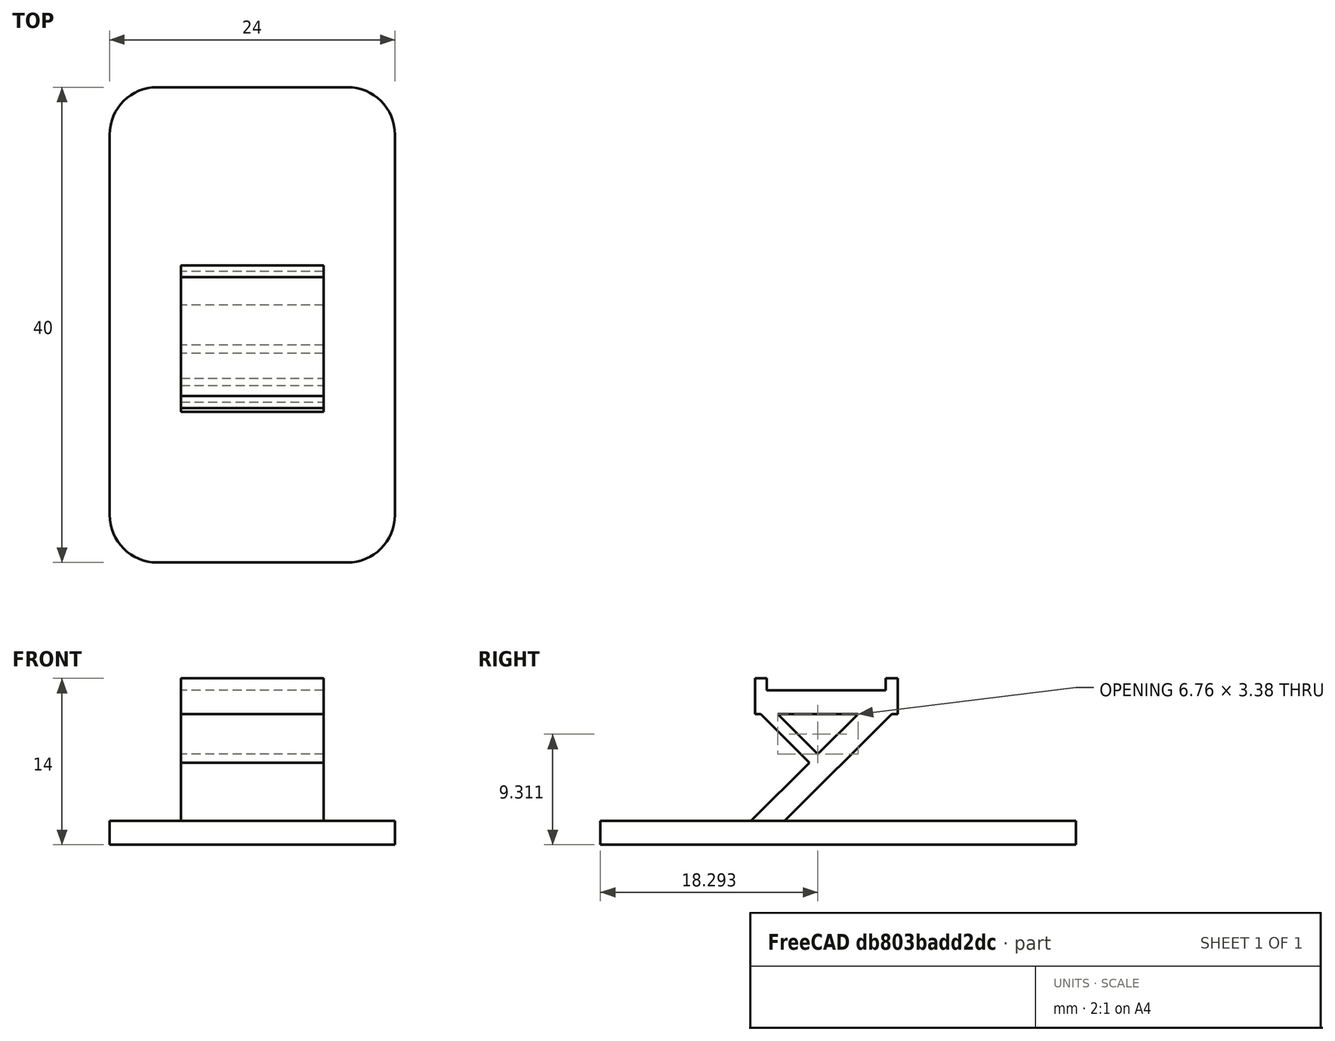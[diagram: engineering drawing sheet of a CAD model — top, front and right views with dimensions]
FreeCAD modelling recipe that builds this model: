
FCSTD DOCUMENT  (FreeCAD 0.17R13528 (Git))
Label: soporte
License: All rights reserved
LicenseURL: http://en.wikipedia.org/wiki/All_rights_reserved
objects: Part::Box×6, Mesh::Feature×1, Part::MultiFuse×1, Part::Fillet×1
note: 8 computed .brp shape members not serialized (recipe doc carries the construction recipe); baked Part::Feature solids carry a one-line shape summary decoded from their .brp

FEATURE [Part::Box] Box  label="Cubo"
  AttacherType = Attacher::AttachEngine3D
  Height = 2
  Length = 12
  Placement = pos=(-6,30.3,3.5) rot=(1,0,0;0.785398rad)
  Width = 15
FEATURE [Mesh::Feature] nave_simple
  Placement = pos=(0,0,26) rot=(1,0,0;-1.5708rad)
FEATURE [Part::Box] Box001  label="Cubo001"
  AttacherType = Attacher::AttachEngine3D
  Height = 2
  Length = 12
  Placement = pos=(-6,29.3,15) rot=(0,0,1;0rad)
  Width = 1
FEATURE [Part::Box] Box002  label="Cubo002"
  AttacherType = Attacher::AttachEngine3D
  Height = 2
  Length = 12
  Placement = pos=(-6,40.3,15) rot=(0,0,1;0rad)
  Width = 1
FEATURE [Part::Box] Box003  label="Cubo003"
  AttacherType = Attacher::AttachEngine3D
  Height = 2
  Length = 12
  Placement = pos=(-6,29.3,14) rot=(0,0,1;0rad)
  Width = 12
FEATURE [Part::Box] Box004  label="Cubo004"
  AttacherType = Attacher::AttachEngine3D
  Height = 2
  Length = 24
  Placement = pos=(-12,16.3,3) rot=(0,0,1;0rad)
  Width = 40
FEATURE [Part::Box] Box005  label="Cubo005"
  AttacherType = Attacher::AttachEngine3D
  Height = 1
  Length = 12
  Placement = pos=(-6,29.3,14.5) rot=(-1,0,0;0.785398rad)
  Width = 7
FEATURE [Part::MultiFuse] Fusion
  Refine = true
  Shapes = -> [Box004,Box,Box005,Box003,Box001,Box002]
FEATURE [Part::Fillet] Fillet
  Base = -> Fusion
  Edges = 4 edges r=4: [Edge1,Edge3,Edge6,Edge15]
